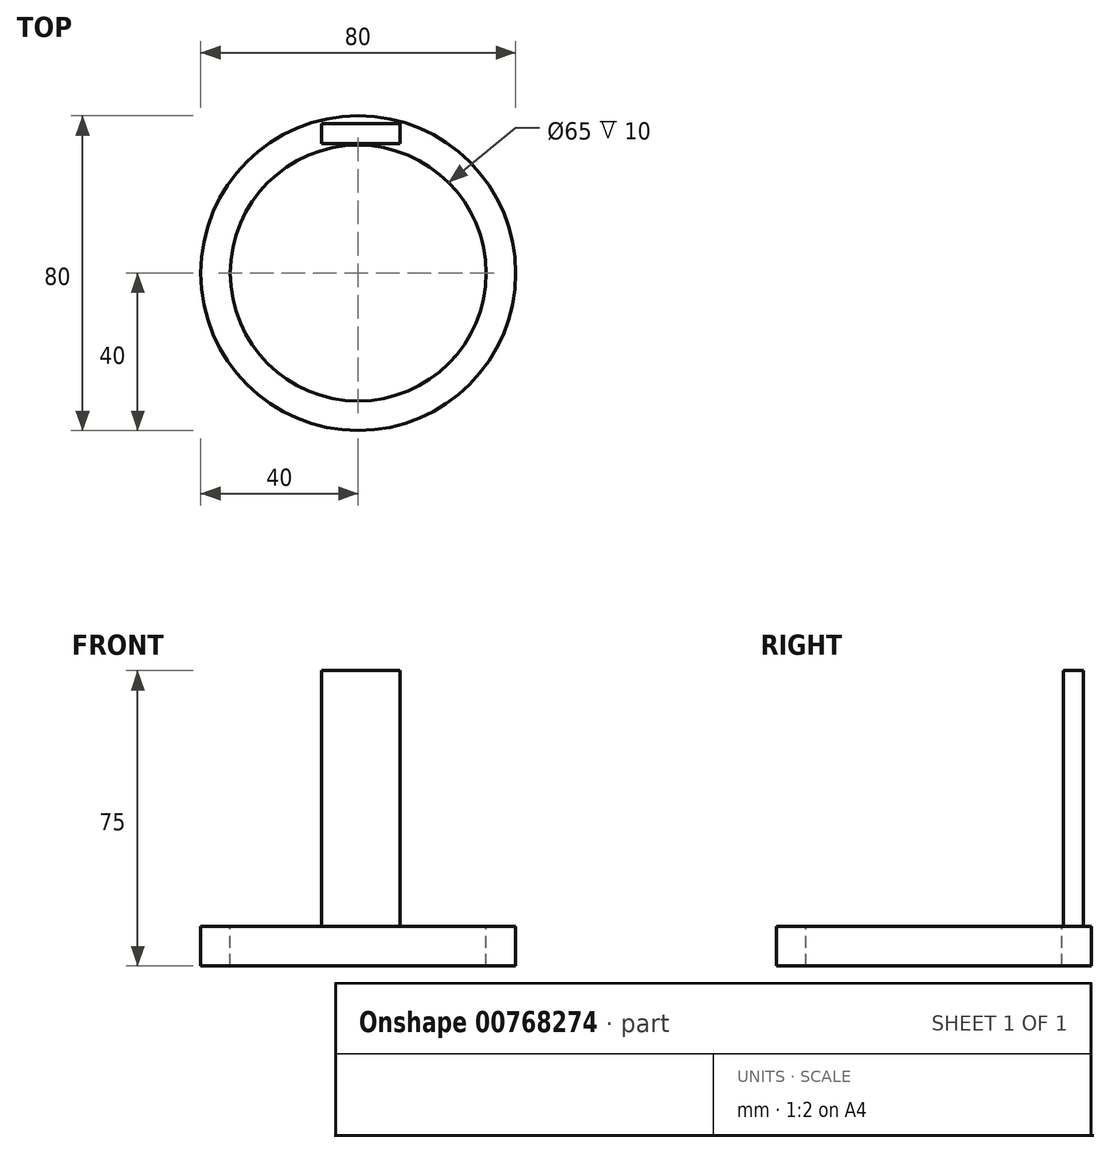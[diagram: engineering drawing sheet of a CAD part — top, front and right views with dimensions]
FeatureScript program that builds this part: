
annotation { "Feature Type Name" : "Feature", "Feature Type Description" : "" }
export const myFeature = defineFeature(function(context is Context, id is Id, definition is map)
    precondition{}
    {
        {
            var Q0;
            Q0=qCreatedBy(makeId("Top.planeOp"),FACE);
            var sketch = newSketch(context, id + "F0", { "sketchPlane" : qUnion([Q0])});
            skCircle(sketch, "E0", {"center": v(0, 0) * mm, "radius": 40 * mm});
            skCircle(sketch, "E1", {"center": v(0, 0) * mm, "radius": 32.5 * mm});
            skSolve(sketch);
        }
        {
            var Q0;
            Q0=makeQuery(id+"F0.imprint","IMPRINT",FACE,{"disambiguationData":[TD([[makeQuery(id+"F0.imprint","IMPRINT",EDGE,{"derivedFrom":sQuery(id+"F0.wireOp",EDGE,"E0")}),1.0]])]});
            extrude(context, id + "F1", {"entities" : qUnion([Q0]), "oppositeDirection" : true, "depth" : 10 * mm, "offsetDistance" : 25 * mm});
        }
        {
            var Q0;
            Q0=qCreatedBy(makeId("Top.planeOp"),FACE);
            var sketch = newSketch(context, id + "F2", { "sketchPlane" : qUnion([Q0])});
            skLineSegment(sketch, "E2.bottom", {"start": v(-9.32, 37.93) * mm, "end": v(10.68, 37.93) * mm});
            skLineSegment(sketch, "E2.top", {"start": v(-9.32, 32.93) * mm, "end": v(10.68, 32.93) * mm});
            skLineSegment(sketch, "E2.left", {"start": v(-9.32, 37.93) * mm, "end": v(-9.32, 32.93) * mm});
            skLineSegment(sketch, "E2.right", {"start": v(10.68, 37.93) * mm, "end": v(10.68, 32.93) * mm});
            skSolve(sketch);
        }
        {
            var Q0;
            Q0=makeQuery(id+"F2.imprint","IMPRINT",FACE,{"disambiguationData":[TD([[makeQuery(id+"F2.imprint","IMPRINT",EDGE,{"derivedFrom":sQuery(id+"F2.wireOp",EDGE,"E2.bottom")}),-1.0]])]});
            extrude(context, id + "F3", {"entities" : qUnion([Q0]), "operationType" : NewBodyOperationType.ADD, "depth" : 65 * mm, "offsetDistance" : 25 * mm});
        }
    });
